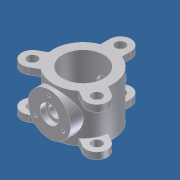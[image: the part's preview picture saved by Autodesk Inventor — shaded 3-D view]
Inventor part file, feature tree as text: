
AUTODESK INVENTOR PART (.ipt)
format: ipt  version: unknown  size: 330,240 bytes
history: native  units: in
note: dims shown in document units (in); Inventor stores cm internally (conversion verified against a paired STEP export)
features: sketch x10, extrude x8, projected_geometry x3, plane x2, hole x2
ambient origin geometry x8: Origin, YZ Plane, XZ Plane, XY Plane, X Axis, Y Axis, Z Axis, Center Point
bodies: Solid1 (feature_tree)
feature tree (25):
  extrude  "Extrusion1"  Depth=2.812in
  extrude  "Extrusion2"  Depth=1.75in
  extrude  "Extrusion3"  Depth=0.47in
  plane  "Work Plane1"
  extrude  "Extrusion4"  Depth=0.47in
  extrude  "Extrusion5"  Depth=0.47in
  extrude  "Extrusion6"  Depth=0.313in TaperAngle=0.0deg
  hole  "Hole1"  [1 undecoded]
  hole  "Hole2"  [1 undecoded]
  plane  "Work Plane3"
  extrude  "Extrusion7"  Depth=1.125in
  extrude  "Extrusion8"  Depth=0.75in
  sketch  "Sketch1"  dims[d0=1.938in d1=2.812in]
  sketch  "Sketch2"  dims[d2=2.25in d3=0.0in d5=1.75in]
  sketch  "Sketch3"  dims[d6=1.0in d7=0.47in]
  projected_geometry  "Projected Loop1"
  projected_geometry  "Projected Loop2"
  projected_geometry  "Projected Loop3"
  sketch  "Sketch5"  dims[d10=1.0in d11=0.47in]
  sketch  "Sketch6"  dims[d15=1.0in d16=0.47in]
  sketch  "Sketch7"  dims[d17=0.313in d18=0.0in d19=0.313in d20=0.0in]
  sketch  "Sketch8"  dims[d21=-1.406in d23=2.0in]
  sketch  "Sketch9"  dims[d24=0.188in d25=0.0in d26=0.42in d27=0.0in]
  sketch  "Sketch10"  dims[d28=0.42in d29=0.0in]
  sketch  "Sketch12"  dims[d30=0.562in d31=0.75in d32=0.875in d33=0.25in d34=0.5635in d35=2.813in d36=0.0in d41=0.156in d42=0.375in d43=0.875in d44=0.25in d45=0.5635in d46=0.375in d47=0.0in d48=1.125in d49=0.75in d50=0.35in d51=0.0in d52=0.25in d53=0.0in]
note: 2 required parameter values undecoded (feature->parameter linkage not recoverable at this tier; creation-order binding heuristic only, values carry confidence <= 0.55)
